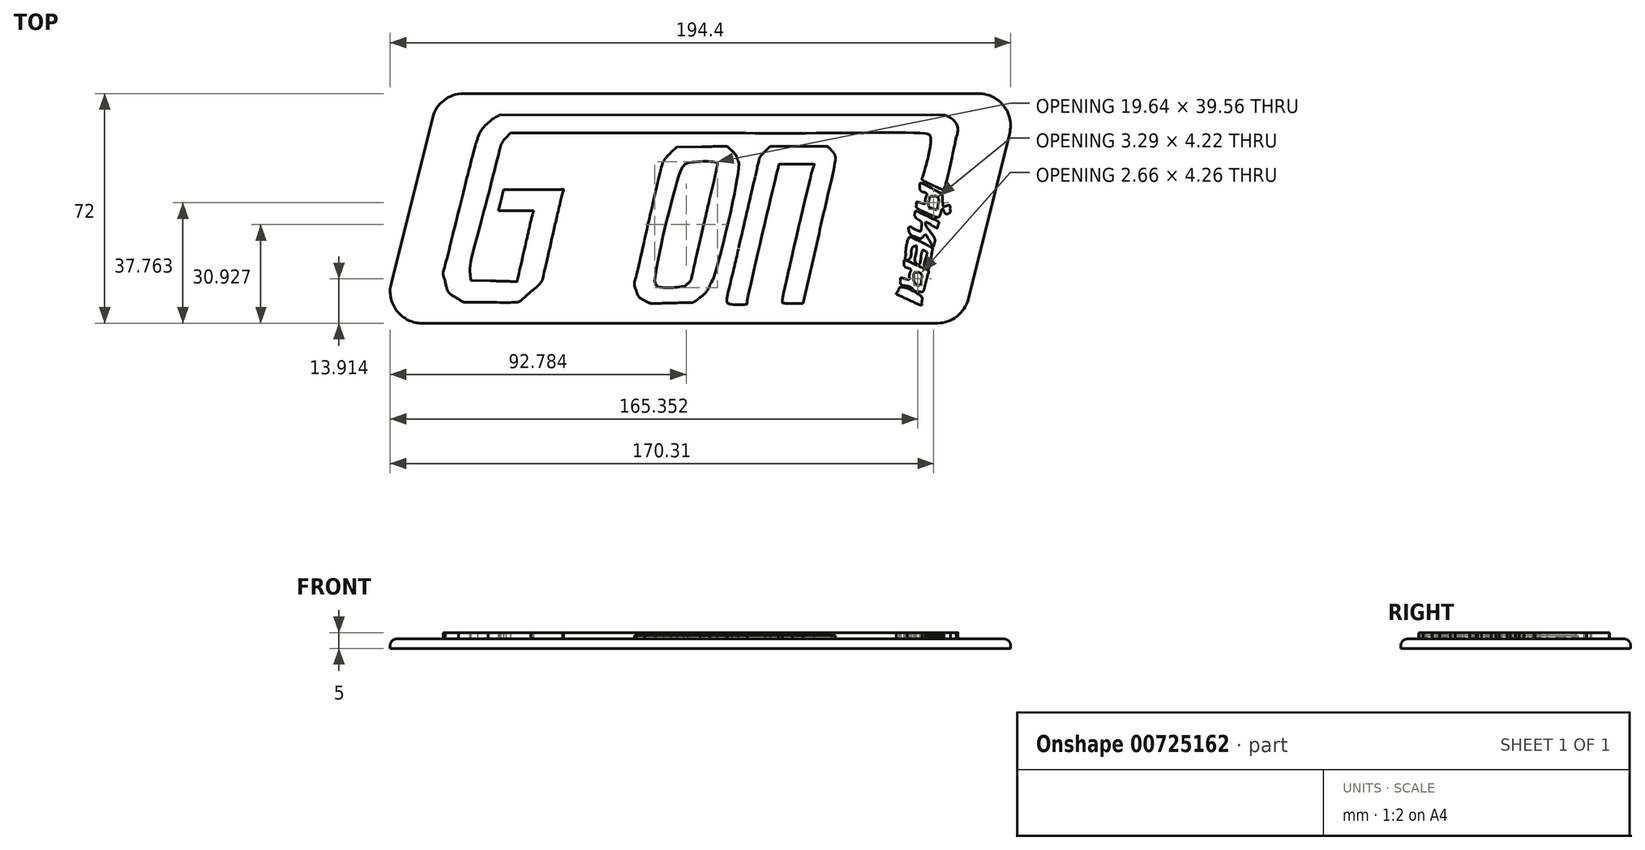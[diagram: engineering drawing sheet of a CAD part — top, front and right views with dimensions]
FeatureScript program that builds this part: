
annotation { "Feature Type Name" : "Feature", "Feature Type Description" : "" }
export const myFeature = defineFeature(function(context is Context, id is Id, definition is map)
    precondition{}
    {
        {
            var Q0;
            Q0=qCreatedBy(makeId("Top.planeOp"),FACE);
            var sketch = newSketch(context, id + "F0", { "sketchPlane" : qUnion([Q0])});
            skLineSegment(sketch, "E0.bottom", {"start": v(-82.05, 36) * mm, "end": v(100, 36) * mm});
            skLineSegment(sketch, "E0.top", {"start": v(-100, -36) * mm, "end": v(82.05, -36) * mm});
            skLineSegment(sketch, "E0.left", {"start": v(-100, 36) * mm, "end": v(-100, -36) * mm, "construction": true});
            skLineSegment(sketch, "E0.right", {"start": v(100, 36) * mm, "end": v(100, -36) * mm, "construction": true});
            skLineSegment(sketch, "E1", {"start": v(-100, -36) * mm, "end": v(-82.05, 36) * mm});
            skLineSegment(sketch, "E2", {"start": v(100, 36) * mm, "end": v(82.05, -36) * mm});
            skSolve(sketch);
        }
        {
            var Q0;
            Q0=makeQuery(id+"F0.imprint","IMPRINT",FACE,{"disambiguationData":[TD([[makeQuery(id+"F0.imprint","IMPRINT",EDGE,{"derivedFrom":sQuery(id+"F0.wireOp",EDGE,"E0.bottom")}),-1.0]])]});
            extrude(context, id + "F1", {"entities" : qUnion([Q0]), "oppositeDirection" : true, "depth" : 3 * mm, "offsetDistance" : 25 * mm});
        }
        {
            var Q0;
            Q0=qCreatedBy(makeId("Top.planeOp"),FACE);
            var sketch = newSketch(context, id + "F2", { "sketchPlane" : qUnion([Q0])});
            skFitSpline(sketch, "E3", {"points": [v(64.81, -28.44) * mm, v(61.47, -26.92) * mm, v(61.38, -26.83) * mm, v(62.1, -25.7) * mm]});
            skFitSpline(sketch, "E4", {"points": [v(62.1, -25.7) * mm, v(62.75, -24.68) * mm, v(69.33, -27.7) * mm, v(69.36, -29.04) * mm]});
            skFitSpline(sketch, "E5", {"points": [v(69.36, -29.04) * mm, v(69.38, -30.3) * mm, v(68.66, -30.2) * mm, v(64.81, -28.44) * mm]});
            skFitSpline(sketch, "E6", {"points": [v(-75.8, -28.42) * mm, v(-78.26, -26.9) * mm, v(-79.25, -25.57) * mm, v(-79.97, -22.8) * mm]});
            skFitSpline(sketch, "E7", {"points": [v(-79.97, -22.8) * mm, v(-80.59, -20.47) * mm, v(-80.34, -19.2) * mm, v(-75.57, -0.14) * mm]});
            skFitSpline(sketch, "E8", {"points": [v(-75.57, -0.14) * mm, v(-72.78, 10.96) * mm, v(-70.21, 20.79) * mm, v(-69.85, 21.7) * mm]});
            skFitSpline(sketch, "E9", {"points": [v(-69.85, 21.7) * mm, v(-68.93, 24.03) * mm, v(-65.2, 27.93) * mm, v(-62.55, 29.35) * mm]});
            skFitSpline(sketch, "E10", {"points": [v(76.47, 29.27) * mm, v(79.26, 27.78) * mm, v(80.7, 25.08) * mm, v(80.15, 22.34) * mm]});
            skFitSpline(sketch, "E11", {"points": [v(80.15, 22.34) * mm, v(79.43, 18.74) * mm, v(76.41, 6.2) * mm, v(76.2, 5.98) * mm]});
            skFitSpline(sketch, "E12", {"points": [v(76.2, 5.98) * mm, v(76.1, 5.85) * mm, v(74.5, 6.46) * mm, v(72.68, 7.33) * mm]});
            skFitSpline(sketch, "E13", {"points": [v(72.68, 7.33) * mm, v(70.32, 8.46) * mm, v(69.44, 9.16) * mm, v(69.62, 9.78) * mm]});
            skFitSpline(sketch, "E14", {"points": [v(69.62, 9.78) * mm, v(70.76, 13.68) * mm, v(72.14, 19.97) * mm, v(72.14, 21.32) * mm]});
            skFitSpline(sketch, "E15", {"points": [v(72.14, 21.32) * mm, v(72.14, 22.31) * mm, v(71.8, 23.1) * mm, v(71.26, 23.3) * mm]});
            skFitSpline(sketch, "E16", {"points": [v(71.26, 23.3) * mm, v(70.78, 23.49) * mm, v(41.16, 23.64) * mm, v(5.43, 23.64) * mm]});
            skLineSegment(sketch, "E17", {"start": v(76.47, 29.27) * mm, "end": v(-62.55, 29.35) * mm});
            skFitSpline(sketch, "E18", {"points": [v(-60.9, 22.17) * mm, v(-61.64, 21.37) * mm, v(-62.48, 19.81) * mm, v(-62.76, 18.72) * mm]});
            skFitSpline(sketch, "E19", {"points": [v(-62.76, 18.72) * mm, v(-69.32, -6.55) * mm, v(-72.23, -18.82) * mm, v(-72.1, -20.5) * mm]});
            skLineSegment(sketch, "E20", {"start": v(5.43, 23.64) * mm, "end": v(-59.53, 23.64) * mm});
            skLineSegment(sketch, "E21", {"start": v(-59.53, 23.64) * mm, "end": v(-60.9, 22.17) * mm});
            skFitSpline(sketch, "E22", {"points": [v(-65.9, -22.7) * mm, v(-57.42, -22.92) * mm, v(-57.41, -22.9) * mm, v(-54.5, -10.1) * mm]});
            skFitSpline(sketch, "E23", {"points": [v(-54.5, -10.1) * mm, v(-53.58, -6) * mm, v(-52.68, -2.2) * mm, v(-52.52, -1.66) * mm]});
            skFitSpline(sketch, "E24", {"points": [v(-52.52, -1.66) * mm, v(-52.25, -0.79) * mm, v(-52.74, -0.7) * mm, v(-57.74, -0.7) * mm]});
            skLineSegment(sketch, "E25", {"start": v(-72.1, -20.5) * mm, "end": v(-71.92, -22.54) * mm});
            skLineSegment(sketch, "E26", {"start": v(-71.92, -22.54) * mm, "end": v(-65.9, -22.7) * mm});
            skFitSpline(sketch, "E27", {"points": [v(-62.8, 1.1) * mm, v(-62.56, 2.1) * mm, v(-62.2, 3.58) * mm, v(-62.01, 4.42) * mm]});
            skLineSegment(sketch, "E28", {"start": v(-57.74, -0.7) * mm, "end": v(-63.26, -0.7) * mm});
            skLineSegment(sketch, "E29", {"start": v(-63.26, -0.7) * mm, "end": v(-62.8, 1.1) * mm});
            skFitSpline(sketch, "E30", {"points": [v(-52.24, 5.94) * mm, v(-43.52, 5.94) * mm, v(-42.84, 5.87) * mm, v(-43.11, 4.97) * mm]});
            skFitSpline(sketch, "E31", {"points": [v(-43.11, 4.97) * mm, v(-43.28, 4.44) * mm, v(-44.66, -1.41) * mm, v(-46.19, -8.03) * mm]});
            skFitSpline(sketch, "E32", {"points": [v(-46.19, -8.03) * mm, v(-49.2, -21.15) * mm, v(-50.07, -23.39) * mm, v(-53.19, -26.12) * mm]});
            skFitSpline(sketch, "E33", {"points": [v(-53.19, -26.12) * mm, v(-56.55, -29.07) * mm, v(-58.08, -29.45) * mm, v(-66.51, -29.45) * mm]});
            skFitSpline(sketch, "E34", {"points": [v(-66.51, -29.45) * mm, v(-72.97, -29.45) * mm, v(-74.4, -29.3) * mm, v(-75.8, -28.42) * mm]});
            skLineSegment(sketch, "E35", {"start": v(-62.01, 4.42) * mm, "end": v(-61.67, 5.94) * mm});
            skLineSegment(sketch, "E36", {"start": v(-61.67, 5.94) * mm, "end": v(-52.24, 5.94) * mm});
            skFitSpline(sketch, "E37", {"points": [v(-43.72, -28.96) * mm, v(-47.34, -27.38) * mm, v(-47.8, -24.3) * mm, v(-45.7, -15.49) * mm]});
            skFitSpline(sketch, "E38", {"points": [v(-41.13, -10.1) * mm, v(-38.26, -10.1) * mm, v(-37.87, -10.22) * mm, v(-38.1, -11.07) * mm]});
            skFitSpline(sketch, "E39", {"points": [v(-38.1, -11.07) * mm, v(-39.27, -15.23) * mm, v(-40.69, -22.54) * mm, v(-40.45, -23.16) * mm]});
            skFitSpline(sketch, "E40", {"points": [v(-40.45, -23.16) * mm, v(-39.99, -24.37) * mm, v(-33.35, -24.2) * mm, v(-32.27, -22.96) * mm]});
            skFitSpline(sketch, "E41", {"points": [v(-32.27, -22.96) * mm, v(-30.96, -21.45) * mm, v(-28.32, -9.06) * mm, v(-29.11, -8.1) * mm]});
            skFitSpline(sketch, "E42", {"points": [v(-29.11, -8.1) * mm, v(-29.46, -7.69) * mm, v(-31.74, -6.28) * mm, v(-34.17, -4.99) * mm]});
            skFitSpline(sketch, "E43", {"points": [v(-34.17, -4.99) * mm, v(-39.14, -2.34) * mm, v(-41.23, -0.25) * mm, v(-41.23, 2.07) * mm]});
            skFitSpline(sketch, "E44", {"points": [v(-41.23, 2.07) * mm, v(-41.23, 4.73) * mm, v(-38.95, 13.86) * mm, v(-37.82, 15.73) * mm]});
            skFitSpline(sketch, "E45", {"points": [v(-37.82, 15.73) * mm, v(-35.85, 19) * mm, v(-33.82, 19.77) * mm, v(-27.24, 19.77) * mm]});
            skFitSpline(sketch, "E46", {"points": [v(-27.24, 19.77) * mm, v(-21.83, 19.77) * mm, v(-21.29, 19.67) * mm, v(-19.77, 18.39) * mm]});
            skFitSpline(sketch, "E47", {"points": [v(-19.77, 18.39) * mm, v(-17.52, 16.5) * mm, v(-17.35, 14.82) * mm, v(-18.73, 8.57) * mm]});
            skLineSegment(sketch, "E48", {"start": v(-45.7, -15.49) * mm, "end": v(-44.41, -10.1) * mm});
            skLineSegment(sketch, "E49", {"start": v(-44.41, -10.1) * mm, "end": v(-41.13, -10.1) * mm});
            skFitSpline(sketch, "E50", {"points": [v(-23.11, 3.18) * mm, v(-25.3, 3.18) * mm, v(-26.3, 3.4) * mm, v(-26.3, 3.87) * mm]});
            skFitSpline(sketch, "E51", {"points": [v(-26.3, 3.87) * mm, v(-26.3, 4.25) * mm, v(-25.8, 6.63) * mm, v(-25.19, 9.16) * mm]});
            skFitSpline(sketch, "E52", {"points": [v(-25.19, 9.16) * mm, v(-24.58, 11.68) * mm, v(-24.09, 13.86) * mm, v(-24.09, 14) * mm]});
            skFitSpline(sketch, "E53", {"points": [v(-24.09, 14) * mm, v(-24.09, 14.13) * mm, v(-25.82, 14.24) * mm, v(-27.94, 14.24) * mm]});
            skFitSpline(sketch, "E54", {"points": [v(-27.94, 14.24) * mm, v(-32.44, 14.24) * mm, v(-32.35, 14.34) * mm, v(-33.74, 7.99) * mm]});
            skFitSpline(sketch, "E55", {"points": [v(-33.74, 7.99) * mm, v(-34.43, 4.84) * mm, v(-34.52, 3.48) * mm, v(-34.08, 2.94) * mm]});
            skFitSpline(sketch, "E56", {"points": [v(-34.08, 2.94) * mm, v(-33.75, 2.54) * mm, v(-31.22, 1.02) * mm, v(-28.47, -0.44) * mm]});
            skFitSpline(sketch, "E57", {"points": [v(-28.47, -0.44) * mm, v(-23.28, -3.2) * mm, v(-21.88, -4.73) * mm, v(-21.88, -7.63) * mm]});
            skFitSpline(sketch, "E58", {"points": [v(-21.88, -7.63) * mm, v(-21.88, -10.07) * mm, v(-25.14, -23.38) * mm, v(-26.17, -25.13) * mm]});
            skFitSpline(sketch, "E59", {"points": [v(-26.17, -25.13) * mm, v(-28, -28.23) * mm, v(-30.33, -29.15) * mm, v(-36.8, -29.3) * mm]});
            skFitSpline(sketch, "E60", {"points": [v(-36.8, -29.3) * mm, v(-40, -29.38) * mm, v(-43.11, -29.23) * mm, v(-43.72, -28.96) * mm]});
            skLineSegment(sketch, "E61", {"start": v(-18.73, 8.57) * mm, "end": v(-19.93, 3.18) * mm});
            skLineSegment(sketch, "E62", {"start": v(-19.93, 3.18) * mm, "end": v(-23.11, 3.18) * mm});
            skFitSpline(sketch, "E63", {"points": [v(-17.45, -28.51) * mm, v(-18.8, -27.82) * mm, v(-19.59, -26.9) * mm, v(-20.05, -25.5) * mm]});
            skFitSpline(sketch, "E64", {"points": [v(-20.05, -25.5) * mm, v(-20.65, -23.65) * mm, v(-20.31, -21.73) * mm, v(-16.4, -4.74) * mm]});
            skFitSpline(sketch, "E65", {"points": [v(-16.4, -4.74) * mm, v(-14.03, 5.56) * mm, v(-11.83, 14.48) * mm, v(-11.5, 15.08) * mm]});
            skFitSpline(sketch, "E66", {"points": [v(-11.5, 15.08) * mm, v(-11.18, 15.68) * mm, v(-10.13, 16.92) * mm, v(-9.17, 17.83) * mm]});
            skFitSpline(sketch, "E67", {"points": [v(0.43, 19.67) * mm, v(8.16, 19.84) * mm, v(8.32, 19.82) * mm, v(9.78, 18.47) * mm]});
            skFitSpline(sketch, "E68", {"points": [v(9.78, 18.47) * mm, v(10.6, 17.71) * mm, v(11.43, 16.4) * mm, v(11.65, 15.56) * mm]});
            skFitSpline(sketch, "E69", {"points": [v(11.65, 15.56) * mm, v(12.07, 13.86) * mm, v(4.67, -19.72) * mm, v(3, -23.7) * mm]});
            skFitSpline(sketch, "E70", {"points": [v(3, -23.7) * mm, v(2.47, -24.96) * mm, v(1.1, -26.7) * mm, v(-0.06, -27.58) * mm]});
            skFitSpline(sketch, "E71", {"points": [v(-0.06, -27.58) * mm, v(-2.07, -29.1) * mm, v(-2.44, -29.18) * mm, v(-8.84, -29.34) * mm]});
            skFitSpline(sketch, "E72", {"points": [v(-8.84, -29.34) * mm, v(-14.4, -29.48) * mm, v(-15.84, -29.35) * mm, v(-17.45, -28.51) * mm]});
            skLineSegment(sketch, "E73", {"start": v(-9.17, 17.83) * mm, "end": v(-7.43, 19.49) * mm});
            skLineSegment(sketch, "E74", {"start": v(-7.43, 19.49) * mm, "end": v(0.43, 19.67) * mm});
            skFitSpline(sketch, "E75", {"points": [v(-3.99, -23.22) * mm, v(-3.3, -22.72) * mm, v(-1.87, -17.52) * mm, v(1.1, -4.65) * mm]});
            skFitSpline(sketch, "E76", {"points": [v(1.1, -4.65) * mm, v(3.37, 5.17) * mm, v(5.22, 13.44) * mm, v(5.22, 13.73) * mm]});
            skFitSpline(sketch, "E77", {"points": [v(5.22, 13.73) * mm, v(5.22, 14.58) * mm, v(-4.5, 14.35) * mm, v(-5.22, 13.48) * mm]});
            skFitSpline(sketch, "E78", {"points": [v(-5.22, 13.48) * mm, v(-6, 12.54) * mm, v(-14.23, -22.77) * mm, v(-13.82, -23.43) * mm]});
            skFitSpline(sketch, "E79", {"points": [v(-13.82, -23.43) * mm, v(-13.34, -24.2) * mm, v(-5.08, -24.02) * mm, v(-3.99, -23.22) * mm]});
            skFitSpline(sketch, "E80", {"points": [v(8.38, -29.04) * mm, v(8.26, -28.81) * mm, v(9.86, -21.28) * mm, v(11.94, -12.3) * mm]});
            skFitSpline(sketch, "E81", {"points": [v(11.94, -12.3) * mm, v(14.02, -3.34) * mm, v(16.37, 6.81) * mm, v(17.17, 10.24) * mm]});
            skFitSpline(sketch, "E82", {"points": [v(17.17, 10.24) * mm, v(18.35, 15.36) * mm, v(18.9, 16.77) * mm, v(20.25, 18.12) * mm]});
            skFitSpline(sketch, "E83", {"points": [v(30.88, 19.77) * mm, v(39.56, 19.77) * mm, v(39.91, 19.72) * mm, v(41.07, 18.49) * mm]});
            skFitSpline(sketch, "E84", {"points": [v(41.07, 18.49) * mm, v(41.73, 17.78) * mm, v(42.28, 16.6) * mm, v(42.28, 15.86) * mm]});
            skFitSpline(sketch, "E85", {"points": [v(42.28, 15.86) * mm, v(42.28, 15.12) * mm, v(40, 4.62) * mm, v(37.2, -7.47) * mm]});
            skLineSegment(sketch, "E86", {"start": v(20.25, 18.12) * mm, "end": v(21.9, 19.77) * mm});
            skLineSegment(sketch, "E87", {"start": v(21.9, 19.77) * mm, "end": v(30.88, 19.77) * mm});
            skFitSpline(sketch, "E88", {"points": [v(28.9, -29.45) * mm, v(27.13, -29.45) * mm, v(25.68, -29.25) * mm, v(25.68, -29.01) * mm]});
            skFitSpline(sketch, "E89", {"points": [v(25.68, -29.01) * mm, v(25.68, -28.51) * mm, v(34.96, 11.78) * mm, v(35.42, 13.27) * mm]});
            skFitSpline(sketch, "E90", {"points": [v(35.42, 13.27) * mm, v(35.69, 14.15) * mm, v(35.2, 14.24) * mm, v(30.2, 14.24) * mm]});
            skFitSpline(sketch, "E91", {"points": [v(30.2, 14.24) * mm, v(24.96, 14.24) * mm, v(24.68, 14.18) * mm, v(24.39, 13) * mm]});
            skFitSpline(sketch, "E92", {"points": [v(24.39, 13) * mm, v(23.66, 10.08) * mm, v(14.62, -28.95) * mm, v(14.62, -29.19) * mm]});
            skFitSpline(sketch, "E93", {"points": [v(14.62, -29.19) * mm, v(14.62, -29.63) * mm, v(8.62, -29.48) * mm, v(8.38, -29.04) * mm]});
            skLineSegment(sketch, "E94", {"start": v(37.2, -7.47) * mm, "end": v(32.13, -29.45) * mm});
            skLineSegment(sketch, "E95", {"start": v(32.13, -29.45) * mm, "end": v(28.9, -29.45) * mm});
            skFitSpline(sketch, "E96", {"points": [v(41.45, -28.96) * mm, v(37.82, -27.38) * mm, v(37.37, -24.3) * mm, v(39.47, -15.49) * mm]});
            skFitSpline(sketch, "E97", {"points": [v(44, -10.1) * mm, v(45.8, -10.1) * mm, v(47.25, -10.2) * mm, v(47.25, -10.32) * mm]});
            skFitSpline(sketch, "E98", {"points": [v(47.25, -10.32) * mm, v(47.25, -10.45) * mm, v(46.62, -13.23) * mm, v(45.85, -16.5) * mm]});
            skFitSpline(sketch, "E99", {"points": [v(45.85, -16.5) * mm, v(45.07, -19.77) * mm, v(44.57, -22.78) * mm, v(44.72, -23.19) * mm]});
            skFitSpline(sketch, "E100", {"points": [v(44.72, -23.19) * mm, v(45.18, -24.37) * mm, v(51.83, -24.18) * mm, v(52.9, -22.96) * mm]});
            skFitSpline(sketch, "E101", {"points": [v(52.9, -22.96) * mm, v(53.37, -22.42) * mm, v(54.43, -19.05) * mm, v(55.25, -15.47) * mm]});
            skFitSpline(sketch, "E102", {"points": [v(55.25, -15.47) * mm, v(56.44, -10.31) * mm, v(56.61, -8.78) * mm, v(56.09, -8.14) * mm]});
            skFitSpline(sketch, "E103", {"points": [v(56.09, -8.14) * mm, v(55.72, -7.7) * mm, v(53.43, -6.28) * mm, v(51, -4.99) * mm]});
            skFitSpline(sketch, "E104", {"points": [v(51, -4.99) * mm, v(46.03, -2.34) * mm, v(43.93, -0.25) * mm, v(43.93, 2.07) * mm]});
            skFitSpline(sketch, "E105", {"points": [v(43.93, 2.07) * mm, v(43.93, 4.73) * mm, v(46.21, 13.86) * mm, v(47.34, 15.73) * mm]});
            skFitSpline(sketch, "E106", {"points": [v(47.34, 15.73) * mm, v(49.34, 19.02) * mm, v(51.33, 19.77) * mm, v(58.14, 19.77) * mm]});
            skFitSpline(sketch, "E107", {"points": [v(58.14, 19.77) * mm, v(64.03, 19.77) * mm, v(64.23, 19.73) * mm, v(65.6, 18.25) * mm]});
            skFitSpline(sketch, "E108", {"points": [v(65.6, 18.25) * mm, v(67.66, 16.03) * mm, v(67.79, 14.67) * mm, v(66.48, 8.62) * mm]});
            skLineSegment(sketch, "E109", {"start": v(39.47, -15.49) * mm, "end": v(40.75, -10.1) * mm});
            skLineSegment(sketch, "E110", {"start": v(40.75, -10.1) * mm, "end": v(44, -10.1) * mm});
            skFitSpline(sketch, "E111", {"points": [v(62.09, 3.18) * mm, v(59.88, 3.18) * mm, v(58.87, 3.4) * mm, v(58.87, 3.87) * mm]});
            skFitSpline(sketch, "E112", {"points": [v(58.87, 3.87) * mm, v(58.87, 4.25) * mm, v(59.37, 6.63) * mm, v(59.98, 9.16) * mm]});
            skFitSpline(sketch, "E113", {"points": [v(59.98, 9.16) * mm, v(60.58, 11.68) * mm, v(61.08, 13.86) * mm, v(61.08, 14) * mm]});
            skFitSpline(sketch, "E114", {"points": [v(61.08, 14) * mm, v(61.08, 14.13) * mm, v(59.33, 14.24) * mm, v(57.2, 14.24) * mm]});
            skFitSpline(sketch, "E115", {"points": [v(57.2, 14.24) * mm, v(52.72, 14.24) * mm, v(52.94, 14.48) * mm, v(51.36, 7.64) * mm]});
            skLineSegment(sketch, "E116", {"start": v(66.48, 8.62) * mm, "end": v(65.31, 3.18) * mm});
            skLineSegment(sketch, "E117", {"start": v(65.31, 3.18) * mm, "end": v(62.09, 3.18) * mm});
            skFitSpline(sketch, "E118", {"points": [v(51.73, 2.47) * mm, v(52.46, 1.87) * mm, v(54.98, 0.42) * mm, v(57.33, -0.76) * mm]});
            skFitSpline(sketch, "E119", {"points": [v(57.33, -0.76) * mm, v(61.8, -3) * mm, v(63.3, -4.72) * mm, v(63.3, -7.63) * mm]});
            skFitSpline(sketch, "E120", {"points": [v(63.3, -7.63) * mm, v(63.3, -10.07) * mm, v(60.03, -23.38) * mm, v(59, -25.13) * mm]});
            skFitSpline(sketch, "E121", {"points": [v(59, -25.13) * mm, v(57.17, -28.23) * mm, v(54.84, -29.15) * mm, v(48.36, -29.3) * mm]});
            skFitSpline(sketch, "E122", {"points": [v(48.36, -29.3) * mm, v(45.17, -29.38) * mm, v(42.05, -29.23) * mm, v(41.45, -28.96) * mm]});
            skLineSegment(sketch, "E123", {"start": v(51.36, 7.64) * mm, "end": v(50.4, 3.54) * mm});
            skLineSegment(sketch, "E124", {"start": v(50.4, 3.54) * mm, "end": v(51.73, 2.47) * mm});
            skFitSpline(sketch, "E125", {"points": [v(66.66, -25.37) * mm, v(66.32, -24.95) * mm, v(65.3, -24.46) * mm, v(64.38, -24.28) * mm]});
            skFitSpline(sketch, "E126", {"points": [v(64.38, -24.28) * mm, v(63.2, -24.04) * mm, v(62.74, -23.63) * mm, v(62.74, -22.82) * mm]});
            skFitSpline(sketch, "E127", {"points": [v(62.74, -22.82) * mm, v(62.74, -21.9) * mm, v(62.98, -21.75) * mm, v(64.12, -22.04) * mm]});
            skFitSpline(sketch, "E128", {"points": [v(64.12, -22.04) * mm, v(65.14, -22.3) * mm, v(65.5, -22.16) * mm, v(65.5, -21.54) * mm]});
            skFitSpline(sketch, "E129", {"points": [v(65.5, -21.54) * mm, v(65.5, -21.08) * mm, v(65.65, -20.32) * mm, v(65.82, -19.87) * mm]});
            skFitSpline(sketch, "E130", {"points": [v(65.82, -19.87) * mm, v(66.02, -19.35) * mm, v(65.71, -18.91) * mm, v(64.99, -18.68) * mm]});
            skFitSpline(sketch, "E131", {"points": [v(64.99, -18.68) * mm, v(64.35, -18.48) * mm, v(63.84, -17.84) * mm, v(63.84, -17.25) * mm]});
            skFitSpline(sketch, "E132", {"points": [v(63.84, -17.25) * mm, v(63.84, -16.66) * mm, v(63.93, -16.18) * mm, v(64.04, -16.18) * mm]});
            skFitSpline(sketch, "E133", {"points": [v(64.04, -16.18) * mm, v(64.15, -16.18) * mm, v(65.9, -16.94) * mm, v(67.95, -17.86) * mm]});
            skFitSpline(sketch, "E134", {"points": [v(67.95, -17.86) * mm, v(70.8, -19.15) * mm, v(71.59, -19.75) * mm, v(71.37, -20.49) * mm]});
            skFitSpline(sketch, "E135", {"points": [v(71.37, -20.49) * mm, v(71.22, -21) * mm, v(70.83, -22.5) * mm, v(70.5, -23.78) * mm]});
            skFitSpline(sketch, "E136", {"points": [v(70.5, -23.78) * mm, v(70, -25.7) * mm, v(69.65, -26.14) * mm, v(68.6, -26.14) * mm]});
            skFitSpline(sketch, "E137", {"points": [v(68.6, -26.14) * mm, v(67.88, -26.14) * mm, v(67.01, -25.8) * mm, v(66.66, -25.37) * mm]});
            skFitSpline(sketch, "E138", {"points": [v(69.28, -22.28) * mm, v(69.45, -21.13) * mm, v(68.65, -20.08) * mm, v(67.58, -20.06) * mm]});
            skFitSpline(sketch, "E139", {"points": [v(67.58, -20.06) * mm, v(67.06, -20.05) * mm, v(67.03, -23.05) * mm, v(67.54, -23.57) * mm]});
            skFitSpline(sketch, "E140", {"points": [v(67.54, -23.57) * mm, v(68.22, -24.24) * mm, v(69.1, -23.6) * mm, v(69.28, -22.28) * mm]});
            skFitSpline(sketch, "E141", {"points": [v(70.35, -18.08) * mm, v(70.18, -17.9) * mm, v(70.28, -16.88) * mm, v(70.58, -15.8) * mm]});
            skFitSpline(sketch, "E142", {"points": [v(70.58, -15.8) * mm, v(71, -14.28) * mm, v(70.95, -13.7) * mm, v(70.39, -13.35) * mm]});
            skFitSpline(sketch, "E143", {"points": [v(70.39, -13.35) * mm, v(69.85, -13.02) * mm, v(69.52, -13.41) * mm, v(69.17, -14.84) * mm]});
            skFitSpline(sketch, "E144", {"points": [v(69.17, -14.84) * mm, v(68.51, -17.55) * mm, v(67.4, -16.94) * mm, v(67.63, -14) * mm]});
            skFitSpline(sketch, "E145", {"points": [v(67.63, -14) * mm, v(67.78, -12.2) * mm, v(67.64, -11.69) * mm, v(67.08, -11.88) * mm]});
            skFitSpline(sketch, "E146", {"points": [v(67.08, -11.88) * mm, v(66.67, -12.01) * mm, v(66.2, -12.83) * mm, v(66.06, -13.7) * mm]});
            skFitSpline(sketch, "E147", {"points": [v(66.06, -13.7) * mm, v(65.71, -15.65) * mm, v(64.4, -16.23) * mm, v(64.4, -14.43) * mm]});
            skFitSpline(sketch, "E148", {"points": [v(64.4, -14.43) * mm, v(64.4, -12.92) * mm, v(65.43, -9) * mm, v(65.82, -9) * mm]});
            skFitSpline(sketch, "E149", {"points": [v(65.82, -9) * mm, v(65.97, -9) * mm, v(67.6, -9.75) * mm, v(69.44, -10.69) * mm]});
            skFitSpline(sketch, "E150", {"points": [v(72.44, -14.42) * mm, v(71.77, -18.22) * mm, v(71.3, -19.03) * mm, v(70.35, -18.08) * mm]});
            skLineSegment(sketch, "E151", {"start": v(69.44, -10.69) * mm, "end": v(72.8, -12.38) * mm});
            skLineSegment(sketch, "E152", {"start": v(72.8, -12.38) * mm, "end": v(72.44, -14.42) * mm});
            skFitSpline(sketch, "E153", {"points": [v(72.18, -10.79) * mm, v(70.78, -8.34) * mm, v(70.6, -8.2) * mm, v(69.75, -8.9) * mm]});
            skFitSpline(sketch, "E154", {"points": [v(69.75, -8.9) * mm, v(69.13, -9.43) * mm, v(68.62, -9.43) * mm, v(67.5, -8.92) * mm]});
            skFitSpline(sketch, "E155", {"points": [v(67.5, -8.92) * mm, v(65.84, -8.16) * mm, v(65.38, -5.85) * mm, v(67.02, -6.48) * mm]});
            skFitSpline(sketch, "E156", {"points": [v(67.02, -6.48) * mm, v(68.78, -7.17) * mm, v(69.07, -7.07) * mm, v(69.27, -5.71) * mm]});
            skFitSpline(sketch, "E157", {"points": [v(69.27, -5.71) * mm, v(69.4, -4.82) * mm, v(69.07, -4.07) * mm, v(68.26, -3.46) * mm]});
            skFitSpline(sketch, "E158", {"points": [v(68.26, -3.46) * mm, v(67.6, -2.95) * mm, v(67.13, -2.13) * mm, v(67.24, -1.62) * mm]});
            skFitSpline(sketch, "E159", {"points": [v(67.24, -1.62) * mm, v(67.41, -0.83) * mm, v(67.92, -0.93) * mm, v(71.1, -2.42) * mm]});
            skFitSpline(sketch, "E160", {"points": [v(71.1, -2.42) * mm, v(74.04, -3.79) * mm, v(74.72, -4.33) * mm, v(74.5, -5.16) * mm]});
            skFitSpline(sketch, "E161", {"points": [v(74.5, -5.16) * mm, v(74.25, -6.12) * mm, v(74.11, -6.13) * mm, v(72.63, -5.37) * mm]});
            skFitSpline(sketch, "E162", {"points": [v(72.63, -5.37) * mm, v(70.66, -4.34) * mm, v(70.57, -5.05) * mm, v(72.35, -7.68) * mm]});
            skFitSpline(sketch, "E163", {"points": [v(72.35, -7.68) * mm, v(73.1, -8.78) * mm, v(73.55, -10.08) * mm, v(73.4, -10.69) * mm]});
            skFitSpline(sketch, "E164", {"points": [v(73.4, -10.69) * mm, v(73.05, -12) * mm, v(72.88, -12.02) * mm, v(72.18, -10.79) * mm]});
            skFitSpline(sketch, "E165", {"points": [v(70.34, -1.16) * mm, v(68.54, -0.37) * mm, v(67.72, 0.33) * mm, v(67.72, 1.04) * mm]});
            skFitSpline(sketch, "E166", {"points": [v(67.72, 1.04) * mm, v(67.72, 1.88) * mm, v(67.99, 2.02) * mm, v(69.1, 1.74) * mm]});
            skFitSpline(sketch, "E167", {"points": [v(69.1, 1.74) * mm, v(70.12, 1.49) * mm, v(70.48, 1.62) * mm, v(70.48, 2.24) * mm]});
            skFitSpline(sketch, "E168", {"points": [v(70.48, 2.24) * mm, v(70.48, 2.7) * mm, v(70.62, 3.46) * mm, v(70.8, 3.9) * mm]});
            skFitSpline(sketch, "E169", {"points": [v(70.8, 3.9) * mm, v(71, 4.43) * mm, v(70.7, 4.87) * mm, v(69.97, 5.1) * mm]});
            skFitSpline(sketch, "E170", {"points": [v(69.97, 5.1) * mm, v(69.31, 5.3) * mm, v(68.82, 5.93) * mm, v(68.82, 6.57) * mm]});
            skFitSpline(sketch, "E171", {"points": [v(68.82, 6.57) * mm, v(68.82, 7.86) * mm, v(69.94, 7.67) * mm, v(73.52, 5.74) * mm]});
            skFitSpline(sketch, "E172", {"points": [v(73.52, 5.74) * mm, v(75.4, 4.72) * mm, v(75.76, 4.24) * mm, v(75.9, 2.54) * mm]});
            skFitSpline(sketch, "E173", {"points": [v(75.9, 2.54) * mm, v(76.04, 0.86) * mm, v(76.25, 0.58) * mm, v(77.15, 0.81) * mm]});
            skFitSpline(sketch, "E174", {"points": [v(77.15, 0.81) * mm, v(77.96, 1.02) * mm, v(78.22, 0.8) * mm, v(78.22, -0.08) * mm]});
            skFitSpline(sketch, "E175", {"points": [v(78.22, -0.08) * mm, v(78.22, -1.33) * mm, v(76.9, -1.68) * mm, v(76.23, -0.6) * mm]});
            skFitSpline(sketch, "E176", {"points": [v(76.23, -0.6) * mm, v(75.96, -0.17) * mm, v(75.68, -0.36) * mm, v(75.38, -1.15) * mm]});
            skFitSpline(sketch, "E177", {"points": [v(75.38, -1.15) * mm, v(74.83, -2.64) * mm, v(73.7, -2.64) * mm, v(70.34, -1.16) * mm]});
            skLineSegment(sketch, "E178", {"start": v(72.18, -10.79) * mm, "end": v(72.18, -10.79) * mm});
            skFitSpline(sketch, "E179", {"points": [v(74.48, 1.21) * mm, v(74.75, 2.61) * mm, v(74.06, 3.73) * mm, v(72.92, 3.73) * mm]});
            skFitSpline(sketch, "E180", {"points": [v(72.92, 3.73) * mm, v(72.08, 3.73) * mm, v(71.59, 0.52) * mm, v(72.38, 0.2) * mm]});
            skFitSpline(sketch, "E181", {"points": [v(72.38, 0.2) * mm, v(73.68, -0.35) * mm, v(74.23, -0.08) * mm, v(74.48, 1.21) * mm]});
            skSolve(sketch);
        }
        {
            var Q0;
            Q0=makeQuery(id+"F2.imprint","IMPRINT",FACE,{"disambiguationData":[TD([[makeQuery(id+"F2.imprint","IMPRINT",EDGE,{"derivedFrom":sQuery(id+"F2.wireOp",EDGE,"E6")}),-1.0]])]});
            var Q1;
            Q1=makeQuery(id+"F2.imprint","IMPRINT",FACE,{"disambiguationData":[TD([[makeQuery(id+"F2.imprint","IMPRINT",EDGE,{"derivedFrom":sQuery(id+"F2.wireOp",EDGE,"E165")}),-1.0]])]});
            var Q2;
            Q2=makeQuery(id+"F2.imprint","IMPRINT",FACE,{"disambiguationData":[TD([[makeQuery(id+"F2.imprint","IMPRINT",EDGE,{"derivedFrom":sQuery(id+"F2.wireOp",EDGE,"E153")}),-1.0]])]});
            var Q3;
            Q3=makeQuery(id+"F2.imprint","IMPRINT",FACE,{"disambiguationData":[TD([[makeQuery(id+"F2.imprint","IMPRINT",EDGE,{"derivedFrom":sQuery(id+"F2.wireOp",EDGE,"E141")}),-1.0]])]});
            var Q4;
            Q4=makeQuery(id+"F2.imprint","IMPRINT",FACE,{"disambiguationData":[TD([[makeQuery(id+"F2.imprint","IMPRINT",EDGE,{"derivedFrom":sQuery(id+"F2.wireOp",EDGE,"E125")}),-1.0]])]});
            var Q5;
            Q5=makeQuery(id+"F2.imprint","IMPRINT",FACE,{"disambiguationData":[TD([[makeQuery(id+"F2.imprint","IMPRINT",EDGE,{"derivedFrom":sQuery(id+"F2.wireOp",EDGE,"E3")}),-1.0]])]});
            extrude(context, id + "F3", {"entities" : qUnion([Q0, Q1, Q2, Q3, Q4, Q5]), "depth" : 2 * mm, "offsetDistance" : 25 * mm});
        }
        {
            var Q0;
            Q0=qCreatedBy(makeId("Top.planeOp"),FACE);
            var sketch = newSketch(context, id + "F4", { "sketchPlane" : qUnion([Q0])});
            skFitSpline(sketch, "E182", {"points": [v(64.81, -28.76) * mm, v(61.47, -27.23) * mm, v(61.38, -27.14) * mm, v(62.1, -26.02) * mm]});
            skFitSpline(sketch, "E183", {"points": [v(62.1, -26.02) * mm, v(62.75, -25) * mm, v(69.33, -28.02) * mm, v(69.36, -29.35) * mm]});
            skFitSpline(sketch, "E184", {"points": [v(69.36, -29.35) * mm, v(69.38, -30.6) * mm, v(68.66, -30.52) * mm, v(64.81, -28.76) * mm]});
            skFitSpline(sketch, "E185", {"points": [v(-75.8, -28.74) * mm, v(-78.26, -27.22) * mm, v(-79.25, -25.88) * mm, v(-79.97, -23.12) * mm]});
            skFitSpline(sketch, "E186", {"points": [v(-79.97, -23.12) * mm, v(-80.59, -20.78) * mm, v(-80.34, -19.52) * mm, v(-75.56, -0.46) * mm]});
            skFitSpline(sketch, "E187", {"points": [v(-75.56, -0.46) * mm, v(-72.78, 10.65) * mm, v(-70.21, 20.48) * mm, v(-69.85, 21.39) * mm]});
            skFitSpline(sketch, "E188", {"points": [v(-69.85, 21.39) * mm, v(-68.93, 23.71) * mm, v(-65.2, 27.62) * mm, v(-62.55, 29.04) * mm]});
            skFitSpline(sketch, "E189", {"points": [v(76.47, 28.96) * mm, v(79.26, 27.47) * mm, v(80.7, 24.76) * mm, v(80.15, 22.02) * mm]});
            skFitSpline(sketch, "E190", {"points": [v(80.15, 22.02) * mm, v(79.43, 18.42) * mm, v(76.41, 5.9) * mm, v(76.2, 5.67) * mm]});
            skFitSpline(sketch, "E191", {"points": [v(76.2, 5.67) * mm, v(76.1, 5.54) * mm, v(74.5, 6.14) * mm, v(72.68, 7.02) * mm]});
            skFitSpline(sketch, "E192", {"points": [v(72.68, 7.02) * mm, v(70.32, 8.14) * mm, v(69.44, 8.85) * mm, v(69.62, 9.46) * mm]});
            skFitSpline(sketch, "E193", {"points": [v(69.62, 9.46) * mm, v(70.76, 13.37) * mm, v(72.14, 19.66) * mm, v(72.14, 21) * mm]});
            skFitSpline(sketch, "E194", {"points": [v(72.14, 21) * mm, v(72.14, 22) * mm, v(71.8, 22.79) * mm, v(71.26, 22.99) * mm]});
            skFitSpline(sketch, "E195", {"points": [v(71.26, 22.99) * mm, v(70.78, 23.17) * mm, v(41.16, 23.32) * mm, v(5.43, 23.32) * mm]});
            skLineSegment(sketch, "E196", {"start": v(-62.55, 29.04) * mm, "end": v(-60.31, 30.24) * mm});
            skLineSegment(sketch, "E197", {"start": v(-60.31, 30.24) * mm, "end": v(6.88, 30.24) * mm});
            skLineSegment(sketch, "E198", {"start": v(6.88, 30.24) * mm, "end": v(74.07, 30.24) * mm});
            skLineSegment(sketch, "E199", {"start": v(74.07, 30.24) * mm, "end": v(76.47, 28.96) * mm});
            skLineSegment(sketch, "E200", {"start": v(76.47, 28.96) * mm, "end": v(-62.55, 29.04) * mm});
            skFitSpline(sketch, "E201", {"points": [v(-60.9, 21.86) * mm, v(-61.64, 21.06) * mm, v(-62.48, 19.5) * mm, v(-62.76, 18.4) * mm]});
            skFitSpline(sketch, "E202", {"points": [v(-62.76, 18.4) * mm, v(-69.32, -6.87) * mm, v(-72.23, -19.13) * mm, v(-72.1, -20.82) * mm]});
            skLineSegment(sketch, "E203", {"start": v(5.43, 23.32) * mm, "end": v(-59.53, 23.32) * mm});
            skLineSegment(sketch, "E204", {"start": v(-59.53, 23.32) * mm, "end": v(-60.9, 21.86) * mm});
            skLineSegment(sketch, "E205", {"start": v(-60.9, 21.86) * mm, "end": v(5.43, 23.32) * mm});
            skFitSpline(sketch, "E206", {"points": [v(-65.9, -23.01) * mm, v(-57.42, -23.23) * mm, v(-57.4, -23.22) * mm, v(-54.5, -10.41) * mm]});
            skFitSpline(sketch, "E207", {"points": [v(-54.5, -10.41) * mm, v(-53.58, -6.3) * mm, v(-52.68, -2.5) * mm, v(-52.52, -1.98) * mm]});
            skFitSpline(sketch, "E208", {"points": [v(-52.52, -1.98) * mm, v(-52.24, -1.1) * mm, v(-52.73, -1) * mm, v(-57.74, -1) * mm]});
            skLineSegment(sketch, "E209", {"start": v(-72.1, -20.82) * mm, "end": v(-71.92, -22.85) * mm});
            skLineSegment(sketch, "E210", {"start": v(-71.92, -22.85) * mm, "end": v(-65.9, -23.01) * mm});
            skLineSegment(sketch, "E211", {"start": v(-65.9, -23.01) * mm, "end": v(-72.1, -20.82) * mm});
            skFitSpline(sketch, "E212", {"points": [v(-62.8, 0.79) * mm, v(-62.56, 1.78) * mm, v(-62.2, 3.27) * mm, v(-62.01, 4.1) * mm]});
            skLineSegment(sketch, "E213", {"start": v(-57.74, -1) * mm, "end": v(-63.26, -1) * mm});
            skLineSegment(sketch, "E214", {"start": v(-63.26, -1) * mm, "end": v(-62.8, 0.79) * mm});
            skLineSegment(sketch, "E215", {"start": v(-62.8, 0.79) * mm, "end": v(-57.74, -1) * mm});
            skFitSpline(sketch, "E216", {"points": [v(-52.24, 5.63) * mm, v(-43.52, 5.63) * mm, v(-42.84, 5.56) * mm, v(-43.11, 4.66) * mm]});
            skFitSpline(sketch, "E217", {"points": [v(-43.11, 4.66) * mm, v(-43.28, 4.13) * mm, v(-44.66, -1.72) * mm, v(-46.19, -8.34) * mm]});
            skFitSpline(sketch, "E218", {"points": [v(-46.19, -8.34) * mm, v(-49.2, -21.46) * mm, v(-50.07, -23.7) * mm, v(-53.19, -26.43) * mm]});
            skFitSpline(sketch, "E219", {"points": [v(-53.19, -26.43) * mm, v(-56.55, -29.38) * mm, v(-58.08, -29.77) * mm, v(-66.51, -29.76) * mm]});
            skFitSpline(sketch, "E220", {"points": [v(-66.51, -29.76) * mm, v(-72.97, -29.76) * mm, v(-74.4, -29.6) * mm, v(-75.8, -28.74) * mm]});
            skLineSegment(sketch, "E221", {"start": v(-62.01, 4.1) * mm, "end": v(-61.67, 5.63) * mm});
            skLineSegment(sketch, "E222", {"start": v(-61.67, 5.63) * mm, "end": v(-52.24, 5.63) * mm});
            skLineSegment(sketch, "E223", {"start": v(-52.24, 5.63) * mm, "end": v(-62.01, 4.1) * mm});
            skFitSpline(sketch, "E224", {"points": [v(-43.72, -29.27) * mm, v(-47.34, -27.7) * mm, v(-47.8, -24.6) * mm, v(-45.7, -15.8) * mm]});
            skFitSpline(sketch, "E225", {"points": [v(-41.13, -10.41) * mm, v(-38.26, -10.41) * mm, v(-37.87, -10.53) * mm, v(-38.1, -11.38) * mm]});
            skFitSpline(sketch, "E226", {"points": [v(-38.1, -11.38) * mm, v(-39.27, -15.55) * mm, v(-40.69, -22.86) * mm, v(-40.45, -23.48) * mm]});
            skFitSpline(sketch, "E227", {"points": [v(-40.45, -23.48) * mm, v(-39.99, -24.68) * mm, v(-33.35, -24.51) * mm, v(-32.27, -23.27) * mm]});
            skFitSpline(sketch, "E228", {"points": [v(-32.27, -23.27) * mm, v(-30.96, -21.76) * mm, v(-28.32, -9.37) * mm, v(-29.11, -8.42) * mm]});
            skFitSpline(sketch, "E229", {"points": [v(-29.11, -8.42) * mm, v(-29.46, -8) * mm, v(-31.74, -6.6) * mm, v(-34.17, -5.3) * mm]});
            skFitSpline(sketch, "E230", {"points": [v(-34.17, -5.3) * mm, v(-39.14, -2.65) * mm, v(-41.23, -0.57) * mm, v(-41.23, 1.76) * mm]});
            skFitSpline(sketch, "E231", {"points": [v(-41.23, 1.76) * mm, v(-41.23, 4.42) * mm, v(-38.95, 13.54) * mm, v(-37.82, 15.42) * mm]});
            skFitSpline(sketch, "E232", {"points": [v(-37.82, 15.42) * mm, v(-35.85, 18.68) * mm, v(-33.82, 19.45) * mm, v(-27.24, 19.45) * mm]});
            skFitSpline(sketch, "E233", {"points": [v(-27.24, 19.45) * mm, v(-21.83, 19.45) * mm, v(-21.29, 19.35) * mm, v(-19.77, 18.08) * mm]});
            skFitSpline(sketch, "E234", {"points": [v(-19.77, 18.08) * mm, v(-17.52, 16.18) * mm, v(-17.35, 14.5) * mm, v(-18.73, 8.25) * mm]});
            skLineSegment(sketch, "E235", {"start": v(-45.7, -15.8) * mm, "end": v(-44.41, -10.41) * mm});
            skLineSegment(sketch, "E236", {"start": v(-44.41, -10.41) * mm, "end": v(-41.13, -10.41) * mm});
            skFitSpline(sketch, "E237", {"points": [v(-23.11, 2.86) * mm, v(-25.3, 2.86) * mm, v(-26.3, 3.08) * mm, v(-26.3, 3.55) * mm]});
            skFitSpline(sketch, "E238", {"points": [v(-26.3, 3.55) * mm, v(-26.3, 3.93) * mm, v(-25.8, 6.31) * mm, v(-25.19, 8.84) * mm]});
            skFitSpline(sketch, "E239", {"points": [v(-25.19, 8.84) * mm, v(-24.58, 11.37) * mm, v(-24.09, 13.55) * mm, v(-24.09, 13.68) * mm]});
            skFitSpline(sketch, "E240", {"points": [v(-24.09, 13.68) * mm, v(-24.09, 13.81) * mm, v(-25.82, 13.92) * mm, v(-27.94, 13.92) * mm]});
            skFitSpline(sketch, "E241", {"points": [v(-27.94, 13.92) * mm, v(-32.44, 13.92) * mm, v(-32.34, 14.03) * mm, v(-33.74, 7.67) * mm]});
            skFitSpline(sketch, "E242", {"points": [v(-33.74, 7.67) * mm, v(-34.43, 4.52) * mm, v(-34.52, 3.16) * mm, v(-34.08, 2.63) * mm]});
            skFitSpline(sketch, "E243", {"points": [v(-34.08, 2.63) * mm, v(-33.75, 2.23) * mm, v(-31.22, 0.7) * mm, v(-28.47, -0.75) * mm]});
            skFitSpline(sketch, "E244", {"points": [v(-28.47, -0.75) * mm, v(-23.28, -3.51) * mm, v(-21.88, -5.04) * mm, v(-21.88, -7.94) * mm]});
            skFitSpline(sketch, "E245", {"points": [v(-21.88, -7.94) * mm, v(-21.88, -10.39) * mm, v(-25.14, -23.7) * mm, v(-26.17, -25.44) * mm]});
            skFitSpline(sketch, "E246", {"points": [v(-26.17, -25.44) * mm, v(-28, -28.54) * mm, v(-30.33, -29.46) * mm, v(-36.8, -29.62) * mm]});
            skFitSpline(sketch, "E247", {"points": [v(-36.8, -29.62) * mm, v(-40, -29.7) * mm, v(-43.11, -29.54) * mm, v(-43.72, -29.27) * mm]});
            skLineSegment(sketch, "E248", {"start": v(-18.73, 8.25) * mm, "end": v(-19.93, 2.86) * mm});
            skLineSegment(sketch, "E249", {"start": v(-19.93, 2.86) * mm, "end": v(-23.11, 2.86) * mm});
            skFitSpline(sketch, "E250", {"points": [v(-17.45, -28.83) * mm, v(-18.8, -28.13) * mm, v(-19.59, -27.22) * mm, v(-20.05, -25.8) * mm]});
            skFitSpline(sketch, "E251", {"points": [v(-20.05, -25.8) * mm, v(-20.65, -23.97) * mm, v(-20.3, -22.04) * mm, v(-16.4, -5.05) * mm]});
            skFitSpline(sketch, "E252", {"points": [v(-16.4, -5.05) * mm, v(-14.03, 5.25) * mm, v(-11.83, 14.17) * mm, v(-11.5, 14.77) * mm]});
            skFitSpline(sketch, "E253", {"points": [v(-11.5, 14.77) * mm, v(-11.18, 15.37) * mm, v(-10.13, 16.6) * mm, v(-9.17, 17.52) * mm]});
            skFitSpline(sketch, "E254", {"points": [v(0.43, 19.35) * mm, v(8.16, 19.53) * mm, v(8.32, 19.5) * mm, v(9.78, 18.16) * mm]});
            skFitSpline(sketch, "E255", {"points": [v(9.78, 18.16) * mm, v(10.6, 17.4) * mm, v(11.43, 16.1) * mm, v(11.65, 15.25) * mm]});
            skFitSpline(sketch, "E256", {"points": [v(11.65, 15.25) * mm, v(12.07, 13.55) * mm, v(4.67, -20.03) * mm, v(3, -24.02) * mm]});
            skFitSpline(sketch, "E257", {"points": [v(3, -24.02) * mm, v(2.47, -25.27) * mm, v(1.1, -27.01) * mm, v(-0.06, -27.9) * mm]});
            skFitSpline(sketch, "E258", {"points": [v(-0.06, -27.9) * mm, v(-2.07, -29.42) * mm, v(-2.44, -29.5) * mm, v(-8.84, -29.66) * mm]});
            skFitSpline(sketch, "E259", {"points": [v(-8.84, -29.66) * mm, v(-14.4, -29.8) * mm, v(-15.84, -29.66) * mm, v(-17.45, -28.83) * mm]});
            skLineSegment(sketch, "E260", {"start": v(-9.17, 17.52) * mm, "end": v(-7.43, 19.18) * mm});
            skLineSegment(sketch, "E261", {"start": v(-7.43, 19.18) * mm, "end": v(0.43, 19.35) * mm});
            skFitSpline(sketch, "E262", {"points": [v(-3.99, -23.54) * mm, v(-3.3, -23.03) * mm, v(-1.87, -17.84) * mm, v(1.1, -4.97) * mm]});
            skFitSpline(sketch, "E263", {"points": [v(1.1, -4.97) * mm, v(3.37, 4.86) * mm, v(5.22, 13.13) * mm, v(5.22, 13.41) * mm]});
            skFitSpline(sketch, "E264", {"points": [v(5.22, 13.41) * mm, v(5.22, 14.27) * mm, v(-4.5, 14.04) * mm, v(-5.22, 13.17) * mm]});
            skFitSpline(sketch, "E265", {"points": [v(-5.22, 13.17) * mm, v(-6, 12.22) * mm, v(-14.23, -23.08) * mm, v(-13.82, -23.75) * mm]});
            skFitSpline(sketch, "E266", {"points": [v(-13.82, -23.75) * mm, v(-13.34, -24.51) * mm, v(-5.08, -24.34) * mm, v(-3.99, -23.54) * mm]});
            skFitSpline(sketch, "E267", {"points": [v(8.38, -29.35) * mm, v(8.26, -29.12) * mm, v(9.86, -21.6) * mm, v(11.94, -12.62) * mm]});
            skFitSpline(sketch, "E268", {"points": [v(11.94, -12.62) * mm, v(14.02, -3.65) * mm, v(16.37, 6.5) * mm, v(17.17, 9.93) * mm]});
            skFitSpline(sketch, "E269", {"points": [v(17.17, 9.93) * mm, v(18.35, 15.04) * mm, v(18.9, 16.46) * mm, v(20.25, 17.8) * mm]});
            skFitSpline(sketch, "E270", {"points": [v(30.88, 19.45) * mm, v(39.56, 19.45) * mm, v(39.91, 19.4) * mm, v(41.07, 18.17) * mm]});
            skFitSpline(sketch, "E271", {"points": [v(41.07, 18.17) * mm, v(41.73, 17.47) * mm, v(42.28, 16.29) * mm, v(42.28, 15.55) * mm]});
            skFitSpline(sketch, "E272", {"points": [v(42.28, 15.55) * mm, v(42.28, 14.8) * mm, v(40, 4.3) * mm, v(37.2, -7.78) * mm]});
            skLineSegment(sketch, "E273", {"start": v(20.25, 17.8) * mm, "end": v(21.9, 19.45) * mm});
            skLineSegment(sketch, "E274", {"start": v(21.9, 19.45) * mm, "end": v(30.88, 19.45) * mm});
            skFitSpline(sketch, "E275", {"points": [v(28.9, -29.77) * mm, v(27.13, -29.77) * mm, v(25.68, -29.57) * mm, v(25.68, -29.33) * mm]});
            skFitSpline(sketch, "E276", {"points": [v(25.68, -29.33) * mm, v(25.68, -28.82) * mm, v(34.96, 11.47) * mm, v(35.42, 12.96) * mm]});
            skFitSpline(sketch, "E277", {"points": [v(35.42, 12.96) * mm, v(35.69, 13.83) * mm, v(35.2, 13.92) * mm, v(30.2, 13.92) * mm]});
            skFitSpline(sketch, "E278", {"points": [v(30.2, 13.92) * mm, v(24.96, 13.92) * mm, v(24.68, 13.86) * mm, v(24.39, 12.68) * mm]});
            skFitSpline(sketch, "E279", {"points": [v(24.39, 12.68) * mm, v(23.66, 9.77) * mm, v(14.62, -29.26) * mm, v(14.62, -29.5) * mm]});
            skFitSpline(sketch, "E280", {"points": [v(14.62, -29.5) * mm, v(14.62, -29.94) * mm, v(8.62, -29.8) * mm, v(8.38, -29.35) * mm]});
            skLineSegment(sketch, "E281", {"start": v(37.2, -7.78) * mm, "end": v(32.13, -29.77) * mm});
            skLineSegment(sketch, "E282", {"start": v(32.13, -29.77) * mm, "end": v(28.9, -29.77) * mm});
            skFitSpline(sketch, "E283", {"points": [v(41.45, -29.27) * mm, v(37.82, -27.7) * mm, v(37.37, -24.6) * mm, v(39.47, -15.8) * mm]});
            skFitSpline(sketch, "E284", {"points": [v(44, -10.41) * mm, v(45.8, -10.41) * mm, v(47.25, -10.51) * mm, v(47.25, -10.64) * mm]});
            skFitSpline(sketch, "E285", {"points": [v(47.25, -10.64) * mm, v(47.25, -10.76) * mm, v(46.62, -13.54) * mm, v(45.85, -16.81) * mm]});
            skFitSpline(sketch, "E286", {"points": [v(45.85, -16.81) * mm, v(45.07, -20.09) * mm, v(44.57, -23.1) * mm, v(44.72, -23.5) * mm]});
            skFitSpline(sketch, "E287", {"points": [v(44.72, -23.5) * mm, v(45.18, -24.68) * mm, v(51.83, -24.5) * mm, v(52.9, -23.27) * mm]});
            skFitSpline(sketch, "E288", {"points": [v(52.9, -23.27) * mm, v(53.37, -22.74) * mm, v(54.43, -19.37) * mm, v(55.25, -15.78) * mm]});
            skFitSpline(sketch, "E289", {"points": [v(55.25, -15.78) * mm, v(56.43, -10.63) * mm, v(56.61, -9.09) * mm, v(56.08, -8.46) * mm]});
            skFitSpline(sketch, "E290", {"points": [v(56.08, -8.46) * mm, v(55.72, -8.01) * mm, v(53.43, -6.6) * mm, v(51, -5.3) * mm]});
            skFitSpline(sketch, "E291", {"points": [v(51, -5.3) * mm, v(46.03, -2.65) * mm, v(43.93, -0.57) * mm, v(43.93, 1.76) * mm]});
            skFitSpline(sketch, "E292", {"points": [v(43.93, 1.76) * mm, v(43.93, 4.42) * mm, v(46.21, 13.54) * mm, v(47.34, 15.42) * mm]});
            skFitSpline(sketch, "E293", {"points": [v(47.34, 15.42) * mm, v(49.34, 18.7) * mm, v(51.33, 19.45) * mm, v(58.14, 19.45) * mm]});
            skFitSpline(sketch, "E294", {"points": [v(58.14, 19.45) * mm, v(64.03, 19.45) * mm, v(64.23, 19.41) * mm, v(65.6, 17.93) * mm]});
            skFitSpline(sketch, "E295", {"points": [v(65.6, 17.93) * mm, v(67.66, 15.71) * mm, v(67.78, 14.36) * mm, v(66.48, 8.3) * mm]});
            skLineSegment(sketch, "E296", {"start": v(39.47, -15.8) * mm, "end": v(40.75, -10.41) * mm});
            skLineSegment(sketch, "E297", {"start": v(40.75, -10.41) * mm, "end": v(44, -10.41) * mm});
            skFitSpline(sketch, "E298", {"points": [v(62.09, 2.86) * mm, v(59.88, 2.86) * mm, v(58.87, 3.08) * mm, v(58.87, 3.55) * mm]});
            skFitSpline(sketch, "E299", {"points": [v(58.87, 3.55) * mm, v(58.87, 3.93) * mm, v(59.37, 6.31) * mm, v(59.98, 8.84) * mm]});
            skFitSpline(sketch, "E300", {"points": [v(59.98, 8.84) * mm, v(60.58, 11.37) * mm, v(61.08, 13.55) * mm, v(61.08, 13.68) * mm]});
            skFitSpline(sketch, "E301", {"points": [v(61.08, 13.68) * mm, v(61.08, 13.81) * mm, v(59.33, 13.92) * mm, v(57.2, 13.92) * mm]});
            skFitSpline(sketch, "E302", {"points": [v(57.2, 13.92) * mm, v(52.72, 13.92) * mm, v(52.94, 14.16) * mm, v(51.36, 7.33) * mm]});
            skLineSegment(sketch, "E303", {"start": v(66.48, 8.3) * mm, "end": v(65.31, 2.86) * mm});
            skLineSegment(sketch, "E304", {"start": v(65.31, 2.86) * mm, "end": v(62.09, 2.86) * mm});
            skFitSpline(sketch, "E305", {"points": [v(51.73, 2.15) * mm, v(52.46, 1.56) * mm, v(54.98, 0.11) * mm, v(57.33, -1.07) * mm]});
            skFitSpline(sketch, "E306", {"points": [v(57.33, -1.07) * mm, v(61.8, -3.32) * mm, v(63.3, -5.04) * mm, v(63.3, -7.94) * mm]});
            skFitSpline(sketch, "E307", {"points": [v(63.3, -7.94) * mm, v(63.3, -10.39) * mm, v(60.03, -23.7) * mm, v(59, -25.44) * mm]});
            skFitSpline(sketch, "E308", {"points": [v(59, -25.44) * mm, v(57.17, -28.54) * mm, v(54.84, -29.46) * mm, v(48.36, -29.62) * mm]});
            skFitSpline(sketch, "E309", {"points": [v(48.36, -29.62) * mm, v(45.16, -29.7) * mm, v(42.05, -29.54) * mm, v(41.45, -29.27) * mm]});
            skLineSegment(sketch, "E310", {"start": v(51.36, 7.33) * mm, "end": v(50.4, 3.23) * mm});
            skLineSegment(sketch, "E311", {"start": v(50.4, 3.23) * mm, "end": v(51.73, 2.15) * mm});
            skFitSpline(sketch, "E312", {"points": [v(66.66, -25.68) * mm, v(66.32, -25.27) * mm, v(65.29, -24.77) * mm, v(64.38, -24.6) * mm]});
            skFitSpline(sketch, "E313", {"points": [v(64.38, -24.6) * mm, v(63.2, -24.36) * mm, v(62.74, -23.94) * mm, v(62.74, -23.13) * mm]});
            skFitSpline(sketch, "E314", {"points": [v(62.74, -23.13) * mm, v(62.74, -22.2) * mm, v(62.98, -22.06) * mm, v(64.12, -22.35) * mm]});
            skFitSpline(sketch, "E315", {"points": [v(64.12, -22.35) * mm, v(65.14, -22.6) * mm, v(65.5, -22.48) * mm, v(65.5, -21.85) * mm]});
            skFitSpline(sketch, "E316", {"points": [v(65.5, -21.85) * mm, v(65.5, -21.39) * mm, v(65.64, -20.64) * mm, v(65.82, -20.18) * mm]});
            skFitSpline(sketch, "E317", {"points": [v(65.82, -20.18) * mm, v(66.02, -19.66) * mm, v(65.71, -19.22) * mm, v(64.99, -19) * mm]});
            skFitSpline(sketch, "E318", {"points": [v(64.99, -19) * mm, v(64.35, -18.8) * mm, v(63.84, -18.16) * mm, v(63.84, -17.56) * mm]});
            skFitSpline(sketch, "E319", {"points": [v(63.84, -17.56) * mm, v(63.84, -16.97) * mm, v(63.93, -16.5) * mm, v(64.04, -16.5) * mm]});
            skFitSpline(sketch, "E320", {"points": [v(64.04, -16.5) * mm, v(64.15, -16.5) * mm, v(65.9, -17.25) * mm, v(67.95, -18.17) * mm]});
            skFitSpline(sketch, "E321", {"points": [v(67.95, -18.17) * mm, v(70.8, -19.47) * mm, v(71.58, -20.07) * mm, v(71.37, -20.8) * mm]});
            skFitSpline(sketch, "E322", {"points": [v(71.37, -20.8) * mm, v(71.22, -21.32) * mm, v(70.83, -22.8) * mm, v(70.5, -24.1) * mm]});
            skFitSpline(sketch, "E323", {"points": [v(70.5, -24.1) * mm, v(70, -26.02) * mm, v(69.65, -26.45) * mm, v(68.6, -26.45) * mm]});
            skFitSpline(sketch, "E324", {"points": [v(68.6, -26.45) * mm, v(67.88, -26.45) * mm, v(67.01, -26.1) * mm, v(66.66, -25.68) * mm]});
            skFitSpline(sketch, "E325", {"points": [v(69.28, -22.6) * mm, v(69.45, -21.44) * mm, v(68.65, -20.4) * mm, v(67.58, -20.37) * mm]});
            skFitSpline(sketch, "E326", {"points": [v(67.58, -20.37) * mm, v(67.06, -20.36) * mm, v(67.03, -23.36) * mm, v(67.54, -23.88) * mm]});
            skFitSpline(sketch, "E327", {"points": [v(67.54, -23.88) * mm, v(68.22, -24.55) * mm, v(69.1, -23.9) * mm, v(69.28, -22.6) * mm]});
            skFitSpline(sketch, "E328", {"points": [v(70.35, -18.4) * mm, v(70.18, -18.22) * mm, v(70.28, -17.19) * mm, v(70.58, -16.1) * mm]});
            skFitSpline(sketch, "E329", {"points": [v(70.58, -16.1) * mm, v(71, -14.59) * mm, v(70.95, -14.02) * mm, v(70.39, -13.67) * mm]});
            skFitSpline(sketch, "E330", {"points": [v(70.39, -13.67) * mm, v(69.85, -13.33) * mm, v(69.52, -13.73) * mm, v(69.17, -15.15) * mm]});
            skFitSpline(sketch, "E331", {"points": [v(69.17, -15.15) * mm, v(68.51, -17.87) * mm, v(67.4, -17.25) * mm, v(67.63, -14.3) * mm]});
            skFitSpline(sketch, "E332", {"points": [v(67.63, -14.3) * mm, v(67.78, -12.51) * mm, v(67.64, -12) * mm, v(67.08, -12.19) * mm]});
            skFitSpline(sketch, "E333", {"points": [v(67.08, -12.19) * mm, v(66.67, -12.33) * mm, v(66.2, -13.14) * mm, v(66.06, -14) * mm]});
            skFitSpline(sketch, "E334", {"points": [v(66.06, -14) * mm, v(65.71, -15.96) * mm, v(64.4, -16.55) * mm, v(64.4, -14.74) * mm]});
            skFitSpline(sketch, "E335", {"points": [v(64.4, -14.74) * mm, v(64.4, -13.24) * mm, v(65.43, -9.3) * mm, v(65.82, -9.3) * mm]});
            skFitSpline(sketch, "E336", {"points": [v(65.82, -9.3) * mm, v(65.97, -9.3) * mm, v(67.6, -10.07) * mm, v(69.44, -11) * mm]});
            skFitSpline(sketch, "E337", {"points": [v(72.44, -14.73) * mm, v(71.77, -18.53) * mm, v(71.3, -19.34) * mm, v(70.35, -18.4) * mm]});
            skLineSegment(sketch, "E338", {"start": v(69.44, -11) * mm, "end": v(72.8, -12.7) * mm});
            skLineSegment(sketch, "E339", {"start": v(72.8, -12.7) * mm, "end": v(72.44, -14.73) * mm});
            skLineSegment(sketch, "E340", {"start": v(72.44, -14.73) * mm, "end": v(69.44, -11) * mm});
            skFitSpline(sketch, "E341", {"points": [v(72.18, -11.1) * mm, v(70.78, -8.66) * mm, v(70.6, -8.52) * mm, v(69.75, -9.22) * mm]});
            skFitSpline(sketch, "E342", {"points": [v(69.75, -9.22) * mm, v(69.12, -9.74) * mm, v(68.62, -9.74) * mm, v(67.5, -9.23) * mm]});
            skFitSpline(sketch, "E343", {"points": [v(67.5, -9.23) * mm, v(65.84, -8.47) * mm, v(65.38, -6.16) * mm, v(67.02, -6.8) * mm]});
            skFitSpline(sketch, "E344", {"points": [v(67.02, -6.8) * mm, v(68.78, -7.48) * mm, v(69.07, -7.38) * mm, v(69.27, -6.03) * mm]});
            skFitSpline(sketch, "E345", {"points": [v(69.27, -6.03) * mm, v(69.4, -5.13) * mm, v(69.07, -4.38) * mm, v(68.26, -3.77) * mm]});
            skFitSpline(sketch, "E346", {"points": [v(68.26, -3.77) * mm, v(67.6, -3.26) * mm, v(67.13, -2.44) * mm, v(67.24, -1.94) * mm]});
            skFitSpline(sketch, "E347", {"points": [v(67.24, -1.94) * mm, v(67.41, -1.14) * mm, v(67.92, -1.25) * mm, v(71.1, -2.73) * mm]});
            skFitSpline(sketch, "E348", {"points": [v(71.1, -2.73) * mm, v(74.04, -4.1) * mm, v(74.72, -4.64) * mm, v(74.5, -5.47) * mm]});
            skFitSpline(sketch, "E349", {"points": [v(74.5, -5.47) * mm, v(74.25, -6.43) * mm, v(74.11, -6.44) * mm, v(72.63, -5.68) * mm]});
            skFitSpline(sketch, "E350", {"points": [v(72.63, -5.68) * mm, v(70.65, -4.66) * mm, v(70.57, -5.36) * mm, v(72.35, -7.99) * mm]});
            skFitSpline(sketch, "E351", {"points": [v(72.35, -7.99) * mm, v(73.1, -9.1) * mm, v(73.55, -10.4) * mm, v(73.4, -11) * mm]});
            skFitSpline(sketch, "E352", {"points": [v(73.4, -11) * mm, v(73.05, -12.32) * mm, v(72.88, -12.33) * mm, v(72.18, -11.1) * mm]});
            skFitSpline(sketch, "E353", {"points": [v(70.34, -1.47) * mm, v(68.54, -0.68) * mm, v(67.71, 0.01) * mm, v(67.71, 0.73) * mm]});
            skFitSpline(sketch, "E354", {"points": [v(67.71, 0.73) * mm, v(67.71, 1.57) * mm, v(67.99, 1.7) * mm, v(69.1, 1.43) * mm]});
            skFitSpline(sketch, "E355", {"points": [v(69.1, 1.43) * mm, v(70.12, 1.17) * mm, v(70.48, 1.3) * mm, v(70.48, 1.93) * mm]});
            skFitSpline(sketch, "E356", {"points": [v(70.48, 1.93) * mm, v(70.48, 2.4) * mm, v(70.62, 3.14) * mm, v(70.8, 3.6) * mm]});
            skFitSpline(sketch, "E357", {"points": [v(70.8, 3.6) * mm, v(71, 4.12) * mm, v(70.7, 4.56) * mm, v(69.97, 4.79) * mm]});
            skFitSpline(sketch, "E358", {"points": [v(69.97, 4.79) * mm, v(69.31, 5) * mm, v(68.82, 5.62) * mm, v(68.82, 6.26) * mm]});
            skFitSpline(sketch, "E359", {"points": [v(68.82, 6.26) * mm, v(68.82, 7.55) * mm, v(69.94, 7.35) * mm, v(73.52, 5.42) * mm]});
            skFitSpline(sketch, "E360", {"points": [v(73.52, 5.42) * mm, v(75.4, 4.41) * mm, v(75.76, 3.93) * mm, v(75.9, 2.22) * mm]});
            skFitSpline(sketch, "E361", {"points": [v(75.9, 2.22) * mm, v(76.04, 0.54) * mm, v(76.24, 0.26) * mm, v(77.15, 0.5) * mm]});
            skFitSpline(sketch, "E362", {"points": [v(77.15, 0.5) * mm, v(77.96, 0.71) * mm, v(78.22, 0.5) * mm, v(78.22, -0.4) * mm]});
            skFitSpline(sketch, "E363", {"points": [v(78.22, -0.4) * mm, v(78.22, -1.64) * mm, v(76.9, -2) * mm, v(76.23, -0.91) * mm]});
            skFitSpline(sketch, "E364", {"points": [v(76.23, -0.91) * mm, v(75.96, -0.48) * mm, v(75.68, -0.67) * mm, v(75.38, -1.47) * mm]});
            skFitSpline(sketch, "E365", {"points": [v(75.38, -1.47) * mm, v(74.83, -2.96) * mm, v(73.7, -2.96) * mm, v(70.34, -1.47) * mm]});
            skLineSegment(sketch, "E366", {"start": v(72.18, -11.1) * mm, "end": v(72.18, -11.1) * mm});
            skFitSpline(sketch, "E367", {"points": [v(74.48, 0.9) * mm, v(74.75, 2.3) * mm, v(74.06, 3.42) * mm, v(72.92, 3.42) * mm]});
            skFitSpline(sketch, "E368", {"points": [v(72.92, 3.42) * mm, v(72.08, 3.42) * mm, v(71.59, 0.2) * mm, v(72.37, -0.12) * mm]});
            skFitSpline(sketch, "E369", {"points": [v(72.37, -0.12) * mm, v(73.68, -0.66) * mm, v(74.23, -0.4) * mm, v(74.48, 0.9) * mm]});
            skSolve(sketch);
        }
        {
            var Q0;
            Q0=makeQuery(id+"F4.imprint","IMPRINT",FACE,{"disambiguationData":[TD([[makeQuery(id+"F4.imprint","IMPRINT",EDGE,{"derivedFrom":sQuery(id+"F4.wireOp",EDGE,"E224")}),-1.0]])]});
            var Q1;
            Q1=makeQuery(id+"F4.imprint","IMPRINT",FACE,{"disambiguationData":[TD([[makeQuery(id+"F4.imprint","IMPRINT",EDGE,{"derivedFrom":sQuery(id+"F4.wireOp",EDGE,"E250")}),-1.0]])]});
            var Q2;
            Q2=makeQuery(id+"F4.imprint","IMPRINT",FACE,{"disambiguationData":[TD([[makeQuery(id+"F4.imprint","IMPRINT",EDGE,{"derivedFrom":sQuery(id+"F4.wireOp",EDGE,"E267")}),-1.0]])]});
            var Q3;
            Q3=makeQuery(id+"F4.imprint","IMPRINT",FACE,{"disambiguationData":[TD([[makeQuery(id+"F4.imprint","IMPRINT",EDGE,{"derivedFrom":sQuery(id+"F4.wireOp",EDGE,"E283")}),-1.0]])]});
            extrude(context, id + "F5", {"entities" : qUnion([Q0, Q1, Q2, Q3]), "depth" : 1 * mm, "offsetDistance" : 25 * mm});
        }
        {
            var Q0;
            Q0=makeQuery(id+"F1.opExtrude","SWEPT_EDGE",EDGE,{"disambiguationData":[OSD([sQuery(id+"F0.wireOp",EDGE,"E0.top"),sQuery(id+"F0.wireOp",EDGE,"E2")])]});
            var Q1;
            Q1=makeQuery(id+"F1.opExtrude","SWEPT_EDGE",EDGE,{"disambiguationData":[OSD([sQuery(id+"F0.wireOp",EDGE,"E0.bottom"),sQuery(id+"F0.wireOp",EDGE,"E2")])]});
            var Q2;
            Q2=makeQuery(id+"F1.opExtrude","SWEPT_EDGE",EDGE,{"disambiguationData":[OSD([sQuery(id+"F0.wireOp",EDGE,"E0.bottom"),sQuery(id+"F0.wireOp",EDGE,"E1")])]});
            var Q3;
            Q3=makeQuery(id+"F1.opExtrude","SWEPT_EDGE",EDGE,{"disambiguationData":[OSD([sQuery(id+"F0.wireOp",EDGE,"E0.top"),sQuery(id+"F0.wireOp",EDGE,"E1")])]});
            fillet(context, id + "F6", {"entities" : qUnion([Q0, Q1, Q2, Q3]), "radius" : 10 * mm, "tangentPropagation" : true, "allowEdgeOverflow" : false});
        }
        {
            var Q0;
            Q0=makeQuery(id+"F1.opExtrude","CAP_FACE",FACE,{"disambiguationData":[OSD([sQuery(id+"F0.wireOp",EDGE,"E0.bottom"),sQuery(id+"F0.wireOp",EDGE,"E0.top"),sQuery(id+"F0.wireOp",EDGE,"E1"),sQuery(id+"F0.wireOp",EDGE,"E2")])],"isStart":true});
            fillet(context, id + "F7", {"entities" : qUnion([Q0]), "radius" : 2 * mm, "tangentPropagation" : true, "allowEdgeOverflow" : false});
        }
    });
